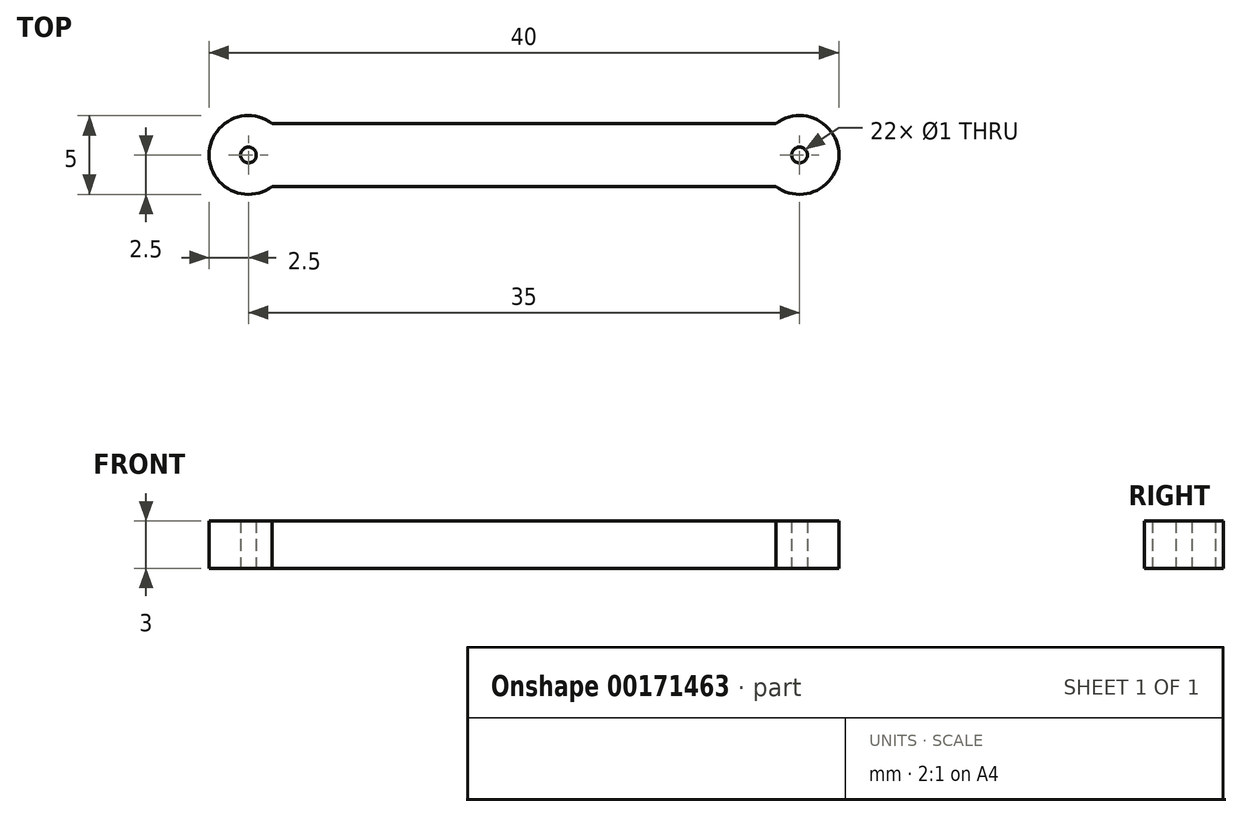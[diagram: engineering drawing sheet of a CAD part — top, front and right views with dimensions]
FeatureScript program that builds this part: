
annotation { "Feature Type Name" : "Feature", "Feature Type Description" : "" }
export const myFeature = defineFeature(function(context is Context, id is Id, definition is map)
    precondition{}
    {
        {
            var Q0;
            Q0=qCreatedBy(makeId("Top.planeOp"),FACE);
            var sketch = newSketch(context, id + "F0", { "sketchPlane" : qUnion([Q0])});
            skLineSegment(sketch, "E0.bottom", {"start": v(17.5, -2) * mm, "end": v(-17.5, -2) * mm});
            skLineSegment(sketch, "E0.top", {"start": v(17.5, 2) * mm, "end": v(-17.5, 2) * mm});
            skLineSegment(sketch, "E0.left", {"start": v(17.5, -2) * mm, "end": v(17.5, 2) * mm});
            skLineSegment(sketch, "E0.right", {"start": v(-17.5, -2) * mm, "end": v(-17.5, 2) * mm});
            skPoint(sketch, "E0.middle", {"position": v(0, 0) * mm});
            skPoint(sketch, "E1", {"position": v(17.5, 0) * mm});
            skCircle(sketch, "E2", {"center": v(17.5, 0) * mm, "radius": 2.5 * mm});
            skCircle(sketch, "E3.MirrorC", {"center": v(-17.5, 0) * mm, "radius": 2.5 * mm});
            skCircle(sketch, "E4", {"center": v(-17.5, 0) * mm, "radius": 0.5 * mm});
            skCircle(sketch, "E5", {"center": v(17.5, 0) * mm, "radius": 0.5 * mm});
            skSolve(sketch);
        }
        {
            var Q0;
            {var subQ0=sQuery(id+"F0.wireOp",EDGE,"E2");var subQ1=sQuery(id+"F0.wireOp",EDGE,"E0.bottom");var subQ2=makeQuery(id+"F0.imprint","INTERSECT",VERTEX,{"derivedFrom":[subQ1,subQ0]});Q0=makeQuery(id+"F0.imprint","IMPRINT",FACE,{"disambiguationData":[TD([[makeQuery(id+"F0.imprint","IMPRINT",EDGE,{"disambiguationData":[TD([[subQ2,-1.0]])],"derivedFrom":subQ1}),-1.0]])]});}
            var Q1;
            {var subQ0=sQuery(id+"F0.wireOp",EDGE,"E0.left");var subQ5=sQuery(id+"F0.wireOp",EDGE,"E0.bottom");var subQ6=makeQuery(id+"F0.imprint","INTERSECT",VERTEX,{"derivedFrom":[subQ5,subQ0]});Q1=makeQuery(id+"F0.imprint","IMPRINT",FACE,{"disambiguationData":[TD([[makeQuery(id+"F0.imprint","IMPRINT",EDGE,{"disambiguationData":[TD([[subQ6,-1.0]])],"derivedFrom":subQ5}),-1.0]])]});}
            var Q2;
            {var subQ0=sQuery(id+"F0.wireOp",EDGE,"E0.left");var subQ5=sQuery(id+"F0.wireOp",EDGE,"E0.bottom");var subQ6=makeQuery(id+"F0.imprint","INTERSECT",VERTEX,{"derivedFrom":[subQ5,subQ0]});Q2=makeQuery(id+"F0.imprint","IMPRINT",FACE,{"disambiguationData":[TD([[makeQuery(id+"F0.imprint","IMPRINT",EDGE,{"disambiguationData":[TD([[subQ6,-1.0]])],"derivedFrom":subQ5}),1.0]])]});}
            var Q3;
            {var subQ0=sQuery(id+"F0.wireOp",EDGE,"E0.right");var subQ5=sQuery(id+"F0.wireOp",EDGE,"E0.bottom");var subQ6=makeQuery(id+"F0.imprint","INTERSECT",VERTEX,{"derivedFrom":[subQ5,subQ0]});Q3=makeQuery(id+"F0.imprint","IMPRINT",FACE,{"disambiguationData":[TD([[makeQuery(id+"F0.imprint","IMPRINT",EDGE,{"disambiguationData":[TD([[subQ6,1.0]])],"derivedFrom":subQ5}),-1.0]])]});}
            var Q4;
            {var subQ0=sQuery(id+"F0.wireOp",EDGE,"E0.right");var subQ5=sQuery(id+"F0.wireOp",EDGE,"E0.bottom");var subQ6=makeQuery(id+"F0.imprint","INTERSECT",VERTEX,{"derivedFrom":[subQ5,subQ0]});Q4=makeQuery(id+"F0.imprint","IMPRINT",FACE,{"disambiguationData":[TD([[makeQuery(id+"F0.imprint","IMPRINT",EDGE,{"disambiguationData":[TD([[subQ6,1.0]])],"derivedFrom":subQ5}),1.0]])]});}
            extrude(context, id + "F1", {"entities" : qUnion([Q0, Q1, Q2, Q3, Q4]), "depth" : 3 * mm});
        }
    });
